# Revit family: Mailboxes_4C-Salsbury_Industries-Surface_Mounted-10_Door_High_Units
name_source: partatom
category: Specialty Equipment
revit_build: Autodesk Revit 2016 (Build: 20190507_1515(x64)
units: mm (PartAtom-declared; Revit-internal decimal feet)

## family parameters
Always vertical = Yes
Cut with Voids When Loaded = No
OmniClass Number = 23.40.90.14.11
OmniClass Title = Mail Boxes
Part Type = Normal
Room Calculation Point = No
Round Connector Dimension = Use Diameter
Shared = No
Work Plane-Based = Yes

## types (9) — shared parameters
4C Unit Depth = 16.450"
4C Unit Height = 37.875"
Assembly Code = C1030910
Assembly Description = Mailboxes
Back Enclosure Material = Aluminum Alloy - Salsbury Finish - Clear (No finish)
Center Divider Offset = 14.381"
Center Extrusion Offset = 0.000"
Decals = Polycarbonate Film - Salsbury Finish - White
Depth = 17.000"
Door Depth = 0.190"
Door Slot R3 = 3700 Series 4C Door Configurations : Empty
Enclosure Opening - Height = 36.625"
Height = 38.500"
Lock Material = Stainless Steel - Salsbury Finish -  Polished
Manufacturer = Salsbury Industries
MasterFormat Number = 10 55 00
MasterFormat Title = Postal Specialties
OmniClass 23 Number = 23.40.90.14.11
OmniClass 23 Title = Mail Boxes
URL = www.mailboxes.com
Version = 5.0 (01/01/21)

## per-type parameters (varying)
- 3810D-10: 4C Unit Width=31.097"; Bottom Back Plate=Yes; Description=10 Door High Unit: 10 MB1, 1 PL4, 1 PL4.5, OM1.5; Door Slot L1=3700 Series 4C Door Configurations : MB1 Door; Door Slot L10=3700 Series 4C Parcel Configurations : PL4 w/ Divider; Door Slot L2=3700 Series 4C Door Configurations : MB1 Door w/ Divider; Door Slot L3=3700 Series 4C Door Configurations : MB1 Door w/ Divider; Door Slot L4=3700 Series 4C Door Configurations : MB1 Door w/ Divider; Door Slot L5=3700 Series 4C Door Configurations : MB1 Door w/ Divider; Door Slot L6=3700 Series 4C Door Configurations : MB1 Door w/ Divider; Door Slot R1=3700 Series 4C Door Configurations : MB1 Door; Door Slot R10=3700 Series 4C Parcel Configurations : PL4.5 w/ Divider; Door Slot R2=3700 Series 4C Door Configurations : MB1 Door w/ Divider; Door Slot R3.5=3700 Series 4C OM1.5 Configuration : OM1.5-FL; Door Slot R4=3700 Series 4C Door Configurations : Empty; Door Slot R4.5=3700 Series 4C Door Configurations : MB1 Door w/ Divider; Door Slot R5=3700 Series 4C Door Configurations : Empty; Door Slot R5.5=3700 Series 4C Door Configurations : MB1 Door w/ Divider; Double Wide Hidden Components=Yes; Enclosure Opening - Width=29.875"; Left Inside Wall=Yes; Right Inside Wall=Yes; Top Back Plate=Yes; Type Comments=Surface Mounted 4C Standard Horizontal Mailbox - Front Loading; Vertical Center Divider=Yes; Width=31.750"
- 3810S-04: 4C Unit Width=16.966"; Bottom Back Plate=No; Description=10 Door High Unit: 4 MB1, 1 PL4.5, OM1.5; Door Slot L1=3700 Series 4C Door Configurations : Empty; Door Slot L10=3700 Series 4C Door Configurations : Empty; Door Slot L2=3700 Series 4C Door Configurations : Empty; Door Slot L3=3700 Series 4C Door Configurations : Empty; Door Slot L4=3700 Series 4C Door Configurations : Empty; Door Slot L5=3700 Series 4C Door Configurations : Empty; Door Slot L6=3700 Series 4C Door Configurations : Empty; Door Slot R1=3700 Series 4C Door Configurations : MB1 Door; Door Slot R10=3700 Series 4C Parcel Configurations : PL4.5 w/ Divider; Door Slot R2=3700 Series 4C Door Configurations : MB1 Door w/ Divider; Door Slot R3.5=3700 Series 4C OM1.5 Configuration : OM1.5-FL; Door Slot R4=3700 Series 4C Door Configurations : Empty; Door Slot R4.5=3700 Series 4C Door Configurations : MB1 Door w/ Divider; Door Slot R5=3700 Series 4C Door Configurations : Empty; Door Slot R5.5=3700 Series 4C Door Configurations : MB1 Door w/ Divider; Double Wide Hidden Components=No; Enclosure Opening - Width=15.750"; Left Inside Wall=No; Right Inside Wall=No; Top Back Plate=No; Type Comments=Surface Mounted 4C Standard Horizontal Mailbox - Front Loading; Vertical Center Divider=No; Width=17.750"
- 3810D-09: 4C Unit Width=31.097"; Bottom Back Plate=Yes; Description=10 Door High Unit: 9 MB1, 1 PL4.5, 1 PL5, OM1.5; Door Slot L1=3700 Series 4C Door Configurations : MB1 Door; Door Slot L10=3700 Series 4C Parcel Configurations : PL5 w/ Divider; Door Slot L2=3700 Series 4C Door Configurations : MB1 Door w/ Divider; Door Slot L3=3700 Series 4C Door Configurations : MB1 Door w/ Divider; Door Slot L4=3700 Series 4C Door Configurations : MB1 Door w/ Divider; Door Slot L5=3700 Series 4C Door Configurations : MB1 Door w/ Divider; Door Slot L6=3700 Series 4C Door Configurations : Empty; Door Slot R1=3700 Series 4C Door Configurations : MB1 Door; Door Slot R10=3700 Series 4C Parcel Configurations : PL4.5 w/ Divider; Door Slot R2=3700 Series 4C Door Configurations : MB1 Door w/ Divider; Door Slot R3.5=3700 Series 4C OM1.5 Configuration : OM1.5-FL; Door Slot R4=3700 Series 4C Door Configurations : Empty; Door Slot R4.5=3700 Series 4C Door Configurations : MB1 Door w/ Divider; Door Slot R5=3700 Series 4C Door Configurations : Empty; Door Slot R5.5=3700 Series 4C Door Configurations : MB1 Door w/ Divider; Double Wide Hidden Components=Yes; Enclosure Opening - Width=29.875"; Left Inside Wall=Yes; Right Inside Wall=Yes; Top Back Plate=Yes; Type Comments=Surface Mounted 4C Standard Horizontal Mailbox - Front Loading; Vertical Center Divider=Yes; Width=31.750"
- 3810D-06: 4C Unit Width=31.097"; Bottom Back Plate=Yes; Description=10 Door High Unit: 6 MB1, 2 PL6, OM2; Door Slot L1=3700 Series 4C Door Configurations : MB1 Door; Door Slot L10=3700 Series 4C Parcel Configurations : PL6 w/ Divider; Door Slot L2=3700 Series 4C Door Configurations : MB1 Door w/ Divider; Door Slot L3=3700 Series 4C Door Configurations : MB1 Door w/ Divider; Door Slot L4=3700 Series 4C Door Configurations : MB1 Door w/ Divider; Door Slot L5=3700 Series 4C Door Configurations : Empty; Door Slot L6=3700 Series 4C Door Configurations : Empty; Door Slot R1=3700 Series 4C Door Configurations : MB1 Door; Door Slot R10=3700 Series 4C Parcel Configurations : PL6 w/ Divider; Door Slot R2=3700 Series 4C Door Configurations : MB1 Door w/ Divider; Door Slot R3.5=3700 Series 4C Door Configurations : Empty; Door Slot R4=3700 Series 4C OM2 Configuration : OM2-FL; Door Slot R4.5=3700 Series 4C Door Configurations : Empty; Door Slot R5=3700 Series 4C Door Configurations : Empty; Door Slot R5.5=3700 Series 4C Door Configurations : Empty; Double Wide Hidden Components=Yes; Enclosure Opening - Width=29.875"; Left Inside Wall=Yes; Right Inside Wall=Yes; Top Back Plate=Yes; Type Comments=Surface Mounted 4C Standard Horizontal Mailbox - Front Loading; Vertical Center Divider=Yes; Width=31.750"
- 3810D-4P: 4C Unit Width=31.097"; Bottom Back Plate=Yes; Description=10 Door High Unit:  4 PL5; Door Slot L1=3700 Series 4C Door Configurations : Empty; Door Slot L10=3700 Series 4C Parcel Configurations : PL5 w/ Divider; Door Slot L2=3700 Series 4C Door Configurations : Empty; Door Slot L3=3700 Series 4C Door Configurations : Empty; Door Slot L4=3700 Series 4C Door Configurations : Empty; Door Slot L5=3700 Series 4C Parcel Configurations : PL5; Door Slot L6=3700 Series 4C Door Configurations : Empty; Door Slot R1=3700 Series 4C Door Configurations : Empty; Door Slot R10=3700 Series 4C Parcel Configurations : PL5 w/ Divider; Door Slot R2=3700 Series 4C Door Configurations : Empty; Door Slot R3.5=3700 Series 4C Door Configurations : Empty; Door Slot R4=3700 Series 4C Door Configurations : Empty; Door Slot R4.5=3700 Series 4C Door Configurations : Empty; Door Slot R5=3700 Series 4C Parcel Configurations : PL5; Door Slot R5.5=3700 Series 4C Door Configurations : Empty; Double Wide Hidden Components=Yes; Enclosure Opening - Width=29.875"; Left Inside Wall=Yes; Right Inside Wall=Yes; Top Back Plate=Yes; Type Comments=Surface Mounted 4C Standard Horizontal Mailbox - Front Loading; Vertical Center Divider=Yes; Width=31.750"
- 3810S-03: 4C Unit Width=16.966"; Bottom Back Plate=No; Description=10 Door High Unit: 3 MB1, 1 PL5, OM2; Door Slot L1=3700 Series 4C Door Configurations : Empty; Door Slot L10=3700 Series 4C Door Configurations : Empty; Door Slot L2=3700 Series 4C Door Configurations : Empty; Door Slot L3=3700 Series 4C Door Configurations : Empty; Door Slot L4=3700 Series 4C Door Configurations : Empty; Door Slot L5=3700 Series 4C Door Configurations : Empty; Door Slot L6=3700 Series 4C Door Configurations : Empty; Door Slot R1=3700 Series 4C Door Configurations : MB1 Door; Door Slot R10=3700 Series 4C Parcel Configurations : PL5 w/ Divider; Door Slot R2=3700 Series 4C Door Configurations : MB1 Door w/ Divider; Door Slot R3.5=3700 Series 4C Door Configurations : Empty; Door Slot R4=3700 Series 4C OM2 Configuration : OM2-FL; Door Slot R4.5=3700 Series 4C Door Configurations : Empty; Door Slot R5=3700 Series 4C Door Configurations : MB1 Door w/ Divider; Door Slot R5.5=3700 Series 4C Door Configurations : Empty; Double Wide Hidden Components=No; Enclosure Opening - Width=15.750"; Left Inside Wall=No; Right Inside Wall=No; Top Back Plate=No; Type Comments=Surface Mounted 4C Standard Horizontal Mailbox - Front Loading; Vertical Center Divider=No; Width=17.750"
- 3810S-2P: 4C Unit Width=16.966"; Bottom Back Plate=No; Description=10 Door High Unit:  2 PL5; Door Slot L1=3700 Series 4C Door Configurations : Empty; Door Slot L10=3700 Series 4C Door Configurations : Empty; Door Slot L2=3700 Series 4C Door Configurations : Empty; Door Slot L3=3700 Series 4C Door Configurations : Empty; Door Slot L4=3700 Series 4C Door Configurations : Empty; Door Slot L5=3700 Series 4C Door Configurations : Empty; Door Slot L6=3700 Series 4C Door Configurations : Empty; Door Slot R1=3700 Series 4C Door Configurations : Empty; Door Slot R10=3700 Series 4C Parcel Configurations : PL5 w/ Divider; Door Slot R2=3700 Series 4C Door Configurations : Empty; Door Slot R3.5=3700 Series 4C Door Configurations : Empty; Door Slot R4=3700 Series 4C Door Configurations : Empty; Door Slot R4.5=3700 Series 4C Door Configurations : Empty; Door Slot R5=3700 Series 4C Parcel Configurations : PL5; Door Slot R5.5=3700 Series 4C Door Configurations : Empty; Double Wide Hidden Components=No; Enclosure Opening - Width=15.750"; Left Inside Wall=No; Right Inside Wall=No; Top Back Plate=No; Type Comments=Surface Mounted 4C Standard Horizontal Mailbox - Front Loading; Vertical Center Divider=No; Width=17.750"
- 3810S-1B: 4C Unit Width=16.966"; Bottom Back Plate=No; Description=10 Door High Unit:  1 Receptacle; Door Slot L1=3700 Series 4C Door Configurations : Empty; Door Slot L10=3700 Series 4C Door Configurations : Empty; Door Slot L2=3700 Series 4C Door Configurations : Empty; Door Slot L3=3700 Series 4C Door Configurations : Empty; Door Slot L4=3700 Series 4C Door Configurations : Empty; Door Slot L5=3700 Series 4C Door Configurations : Empty; Door Slot L6=3700 Series 4C Door Configurations : Empty; Door Slot R1=3700 Series 4C Door Configurations : Empty; Door Slot R10=4C-10 Door High Receptacle; Door Slot R2=3700 Series 4C Door Configurations : Empty; Door Slot R3.5=3700 Series 4C Door Configurations : Empty; Door Slot R4=3700 Series 4C Door Configurations : Empty; Door Slot R4.5=3700 Series 4C Door Configurations : Empty; Door Slot R5=3700 Series 4C Door Configurations : Empty; Door Slot R5.5=3700 Series 4C Door Configurations : Empty; Double Wide Hidden Components=No; Enclosure Opening - Width=15.750"; Left Inside Wall=No; Right Inside Wall=No; Top Back Plate=No; Type Comments=Surface Mounted 4C Standard Horizontal Receptacle Bin - Front Loading; Vertical Center Divider=No; Width=17.750"
- 3810S-1C: 4C Unit Width=16.966"; Bottom Back Plate=No; Description=10 Door High Unit:  1 Collection Box; Door Slot L1=3700 Series 4C Door Configurations : Empty; Door Slot L10=3700 Series 4C Door Configurations : Empty; Door Slot L2=3700 Series 4C Door Configurations : Empty; Door Slot L3=3700 Series 4C Door Configurations : Empty; Door Slot L4=3700 Series 4C Door Configurations : Empty; Door Slot L5=3700 Series 4C Door Configurations : Empty; Door Slot L6=3700 Series 4C Door Configurations : Empty; Door Slot R1=3700 Series 4C Door Configurations : Empty; Door Slot R10=4C-10 Door High Collection Box; Door Slot R2=3700 Series 4C Door Configurations : Empty; Door Slot R3.5=3700 Series 4C Door Configurations : Empty; Door Slot R4=3700 Series 4C Door Configurations : Empty; Door Slot R4.5=3700 Series 4C Door Configurations : Empty; Door Slot R5=3700 Series 4C Door Configurations : Empty; Door Slot R5.5=3700 Series 4C Door Configurations : Empty; Double Wide Hidden Components=No; Enclosure Opening - Width=15.750"; Left Inside Wall=No; Right Inside Wall=No; Top Back Plate=No; Type Comments=Surface Mounted 4C Standard Horizontal Collection Box - Front Loading; Vertical Center Divider=No; Width=17.750"

note: column(s) folded — value = type name in every type: Model

## geometry (parser evidence)
native form markers: Extrusion x5, Sweep x34
no freeform markers — native parametric forms only
